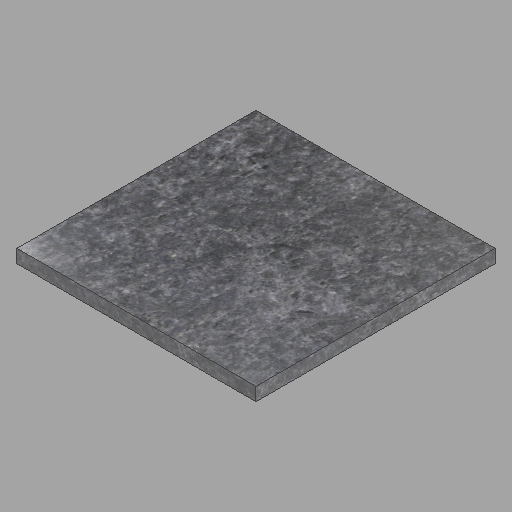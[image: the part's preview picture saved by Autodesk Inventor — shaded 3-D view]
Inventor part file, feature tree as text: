
AUTODESK INVENTOR PART (.ipt)
format: ipt  version: 2023 (Build 270158000, 158)  size: 248,320 bytes
history: native  units: in
note: dims shown in document units (in); Inventor stores cm internally (conversion verified against a paired STEP export)
features: other x1, extrude x1, sketch x1
ambient origin geometry x8: Origin, YZ Plane, XZ Plane, XY Plane, X Axis, Y Axis, Z Axis, Center Point
bodies: Solid1 (feature_tree)
feature tree (3):
  other  "18x18x2-77"
  extrude  "Extrusion1"  Depth=18.0in
  sketch  "Sketch1"  dims[d0=18.0in d1=18.0in d2=1.0in d3=0.0in]
